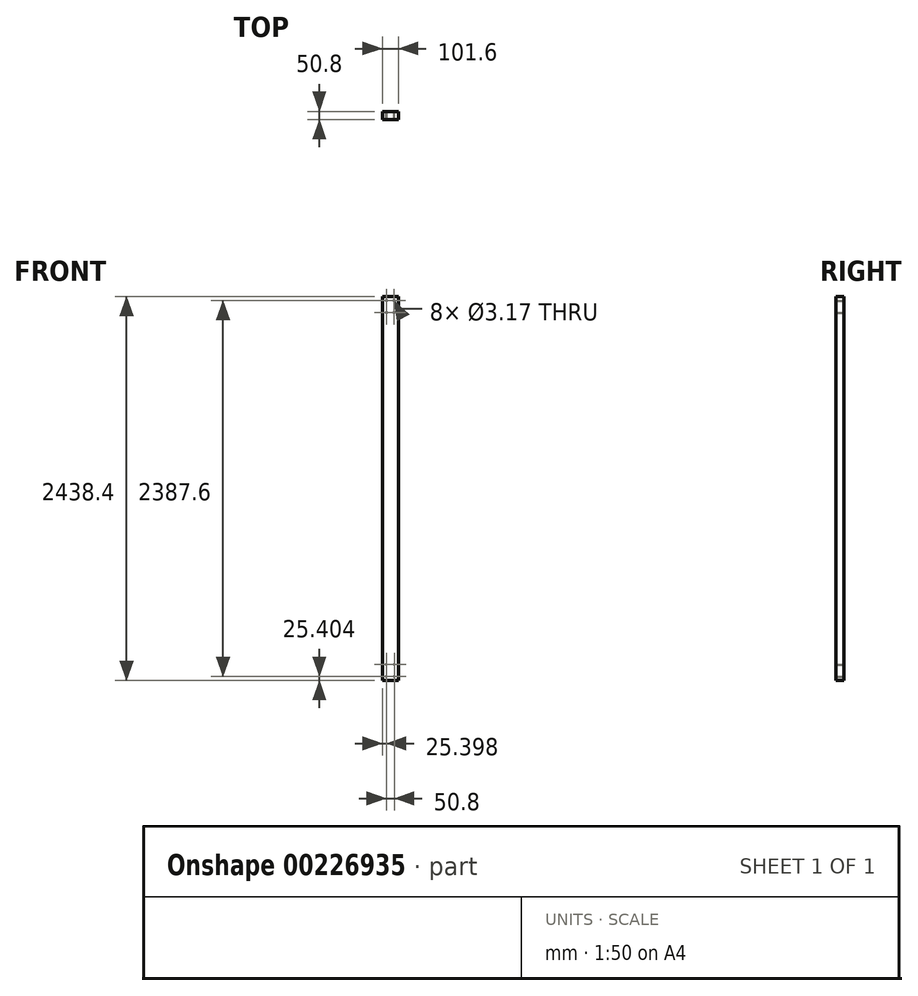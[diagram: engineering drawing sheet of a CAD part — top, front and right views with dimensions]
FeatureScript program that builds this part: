
annotation { "Feature Type Name" : "Feature", "Feature Type Description" : "" }
export const myFeature = defineFeature(function(context is Context, id is Id, definition is map)
    precondition{}
    {
        {
            var Q0;
            Q0=qCreatedBy(makeId("Front.planeOp"),FACE);
            var sketch = newSketch(context, id + "F0", { "sketchPlane" : qUnion([Q0])});
            skLineSegment(sketch, "E0.bottom", {"start": v(-104.31, 2053.3) * mm, "end": v(-2.71, 2053.3) * mm});
            skLineSegment(sketch, "E0.top", {"start": v(-104.31, -385.1) * mm, "end": v(-2.71, -385.1) * mm});
            skLineSegment(sketch, "E0.left", {"start": v(-104.31, 2053.3) * mm, "end": v(-104.31, -385.1) * mm});
            skLineSegment(sketch, "E0.right", {"start": v(-2.71, 2053.3) * mm, "end": v(-2.71, -385.1) * mm});
            skCircle(sketch, "E1", {"center": v(-77.32, 2027.9) * mm, "radius": 1.59 * mm});
            skCircle(sketch, "E2", {"center": v(-29.7, 2027.9) * mm, "radius": 1.59 * mm});
            skCircle(sketch, "E3", {"center": v(-77.32, 1951.7) * mm, "radius": 1.59 * mm});
            skCircle(sketch, "E4", {"center": v(-29.7, 1951.7) * mm, "radius": 1.59 * mm});
            skCircle(sketch, "E5", {"center": v(-78.91, -359.7) * mm, "radius": 1.59 * mm});
            skCircle(sketch, "E6", {"center": v(-28.11, -359.7) * mm, "radius": 1.59 * mm});
            skCircle(sketch, "E7", {"center": v(-28.11, -283.5) * mm, "radius": 1.59 * mm});
            skCircle(sketch, "E8", {"center": v(-78.91, -283.5) * mm, "radius": 1.59 * mm});
            skSolve(sketch);
        }
        {
            var Q0;
            Q0=makeQuery(id+"F0.imprint","IMPRINT",FACE,{"disambiguationData":[TD([[makeQuery(id+"F0.imprint","IMPRINT",EDGE,{"derivedFrom":sQuery(id+"F0.wireOp",EDGE,"E0.bottom")}),-1.0]])]});
            extrude(context, id + "F1", {"entities" : qUnion([Q0]), "depth" : 50.8 * mm});
        }
    });
